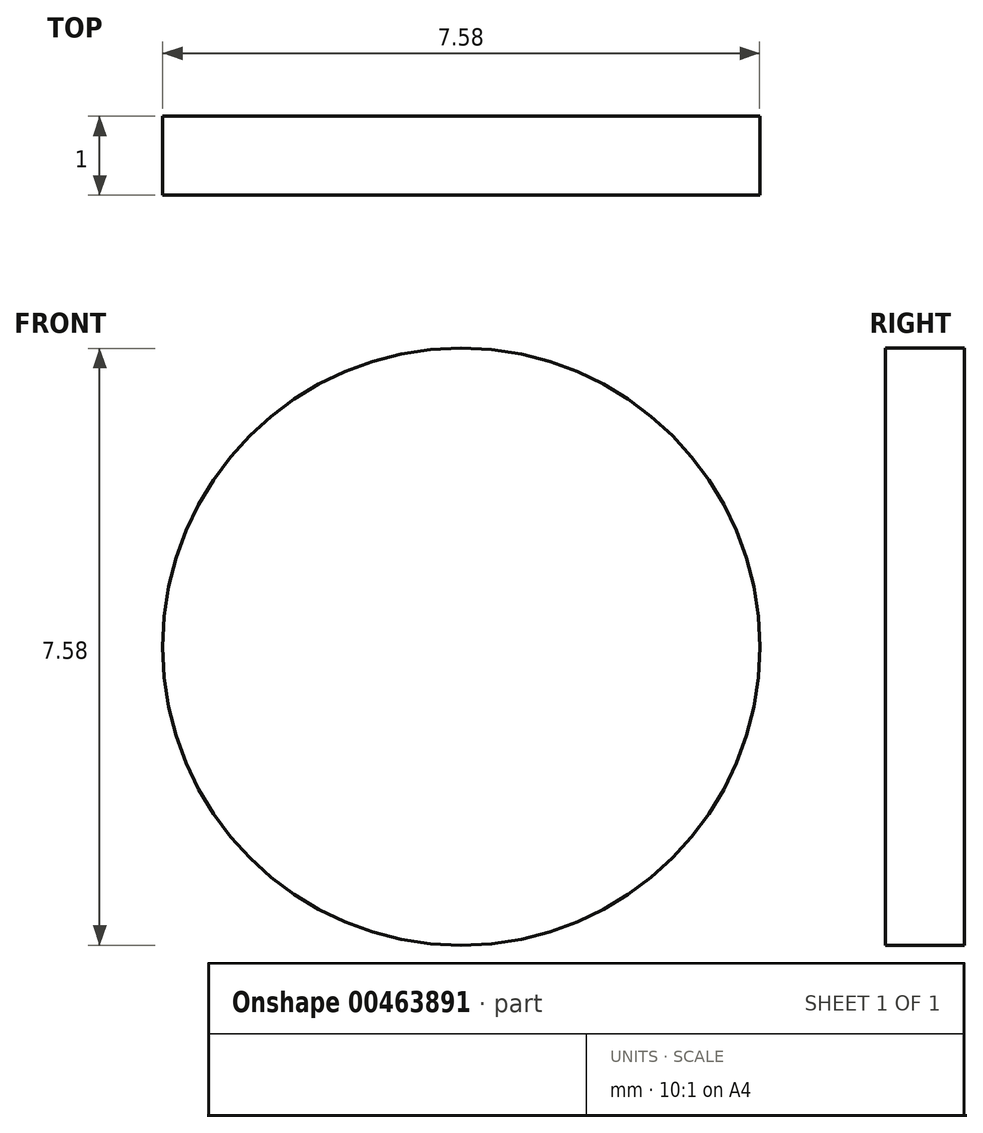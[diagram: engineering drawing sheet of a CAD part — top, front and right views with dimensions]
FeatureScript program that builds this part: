
annotation { "Feature Type Name" : "Feature", "Feature Type Description" : "" }
export const myFeature = defineFeature(function(context is Context, id is Id, definition is map)
    precondition{}
    {
        {
            var Q0;
            Q0=qCreatedBy(makeId("Front.planeOp"),FACE);
            var sketch = newSketch(context, id + "F0", { "sketchPlane" : qUnion([Q0])});
            skCircle(sketch, "E0", {"center": v(0, 0) * mm, "radius": 3.8 * mm});
            skSolve(sketch);
        }
        {
            var Q0;
            Q0 = qSketchRegion(id + "F0", true);
            extrude(context, id + "F1", {"entities" : qUnion([Q0]), "depth" : 1 * mm});
        }
    });
